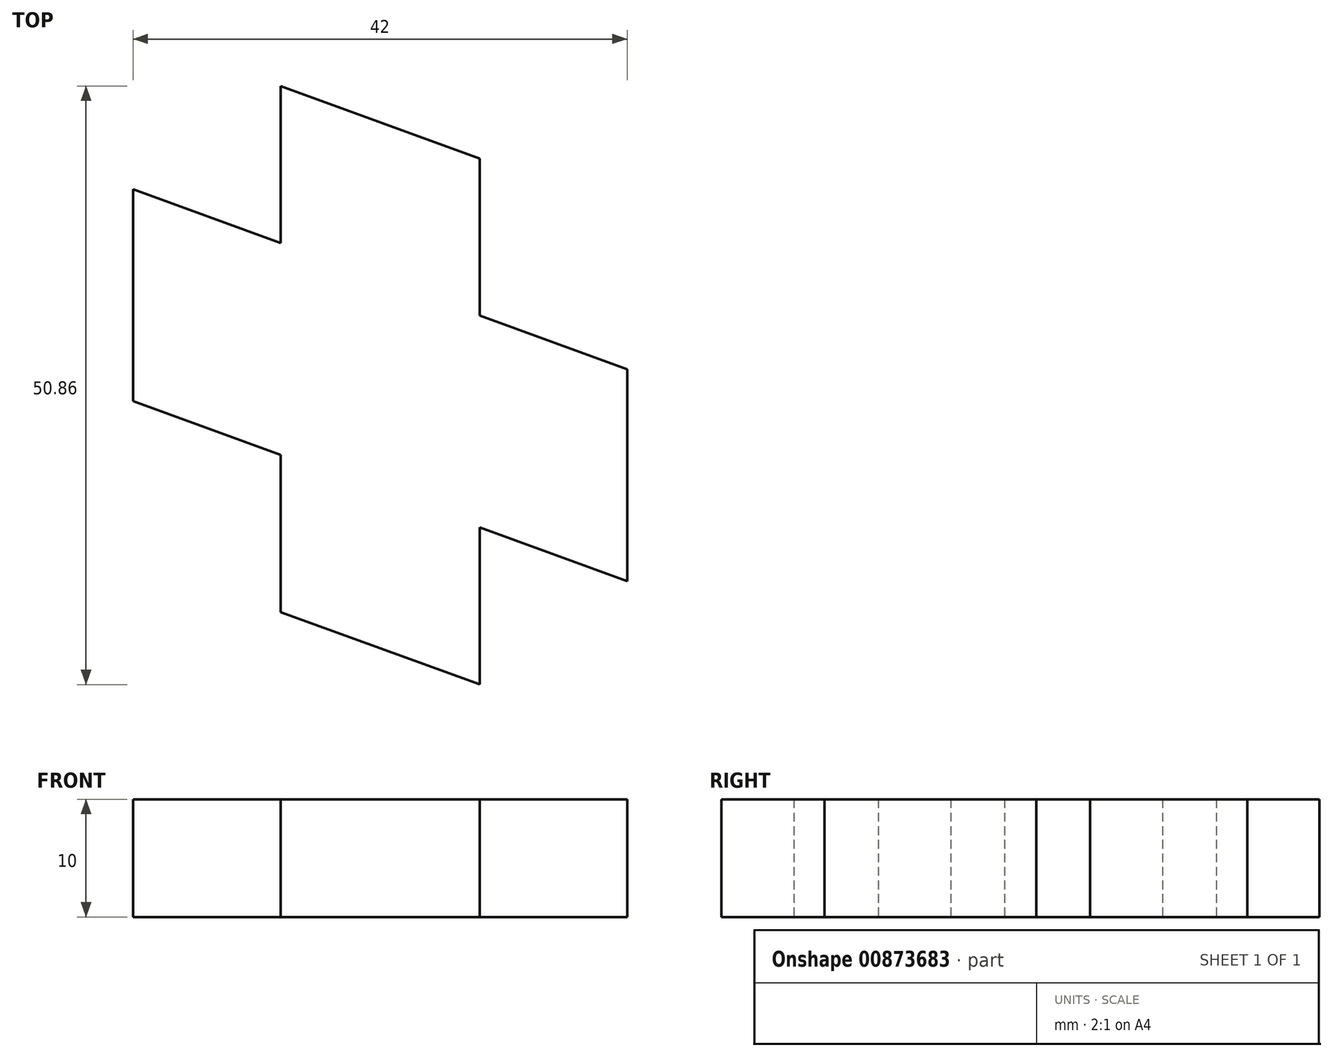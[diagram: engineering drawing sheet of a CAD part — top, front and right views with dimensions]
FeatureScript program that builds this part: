
annotation { "Feature Type Name" : "Feature", "Feature Type Description" : "" }
export const myFeature = defineFeature(function(context is Context, id is Id, definition is map)
    precondition{}
    {
        {
            var Q0;
            Q0=qCreatedBy(makeId("Top.planeOp"),FACE);
            var sketch = newSketch(context, id + "F0", { "sketchPlane" : qUnion([Q0])});
            skLineSegment(sketch, "E0.bottom", {"start": v(21, 9) * mm, "end": v(-21, 9) * mm, "construction": true});
            skLineSegment(sketch, "E0.top", {"start": v(21, -9) * mm, "end": v(-21, -9) * mm, "construction": true});
            skLineSegment(sketch, "E0.left", {"start": v(21, 9) * mm, "end": v(21, -9) * mm, "construction": true});
            skLineSegment(sketch, "E0.right", {"start": v(-21, 9) * mm, "end": v(-21, -9) * mm, "construction": true});
            skPoint(sketch, "E0.middle", {"position": v(0, 0) * mm});
            skLineSegment(sketch, "E1.bottom", {"start": v(-9, 21) * mm, "end": v(9, 21) * mm, "construction": true});
            skLineSegment(sketch, "E1.top", {"start": v(-9, -21) * mm, "end": v(9, -21) * mm, "construction": true});
            skLineSegment(sketch, "E1.left", {"start": v(-9, 21) * mm, "end": v(-9, -21) * mm, "construction": true});
            skLineSegment(sketch, "E1.right", {"start": v(9, 21) * mm, "end": v(9, -21) * mm, "construction": true});
            skPoint(sketch, "E2", {"position": v(-9, 9) * mm});
            skSolve(sketch);
        }
        {
            var Q0;
            Q0=qCreatedBy(makeId("Top.planeOp"),FACE);
            var sketch = newSketch(context, id + "F1", { "sketchPlane" : qUnion([Q0])});
            skLineSegment(sketch, "E3", {"start": v(21, 1.36) * mm, "end": v(21, -16.64) * mm});
            skLineSegment(sketch, "E4", {"start": v(-21, -1.36) * mm, "end": v(-21, 16.64) * mm});
            skLineSegment(sketch, "E5", {"start": v(-21, 16.64) * mm, "end": v(-8.46, 12.08) * mm});
            skLineSegment(sketch, "E6", {"start": v(21, -16.64) * mm, "end": v(8.46, -12.08) * mm});
            skLineSegment(sketch, "E7", {"start": v(-21, 7.64) * mm, "end": v(21, -7.64) * mm, "construction": true});
            skLineSegment(sketch, "E8", {"start": v(-8.46, 12.08) * mm, "end": v(-8.46, 25.43) * mm});
            skLineSegment(sketch, "E9", {"start": v(-8.46, 25.43) * mm, "end": v(8.46, 19.27) * mm});
            skLineSegment(sketch, "E10", {"start": v(8.46, 19.27) * mm, "end": v(8.46, 5.92) * mm});
            skLineSegment(sketch, "E11.trimOffspring", {"start": v(8.46, 5.92) * mm, "end": v(21, 1.36) * mm});
            skLineSegment(sketch, "E12", {"start": v(-8.46, -5.92) * mm, "end": v(-8.46, -19.27) * mm});
            skLineSegment(sketch, "E13", {"start": v(-8.46, -19.27) * mm, "end": v(8.46, -25.43) * mm});
            skLineSegment(sketch, "E14", {"start": v(8.46, -25.43) * mm, "end": v(8.46, -12.08) * mm});
            skLineSegment(sketch, "E15.trimOffspring", {"start": v(-8.46, -5.92) * mm, "end": v(-21, -1.36) * mm});
            skSolve(sketch);
        }
        {
            var Q0;
            Q0 = qSketchRegion(id + "F1", true);
            extrude(context, id + "F2", {"entities" : qUnion([Q0]), "depth" : 10 * mm, "offsetDistance" : 25.4 * mm});
        }
    });
